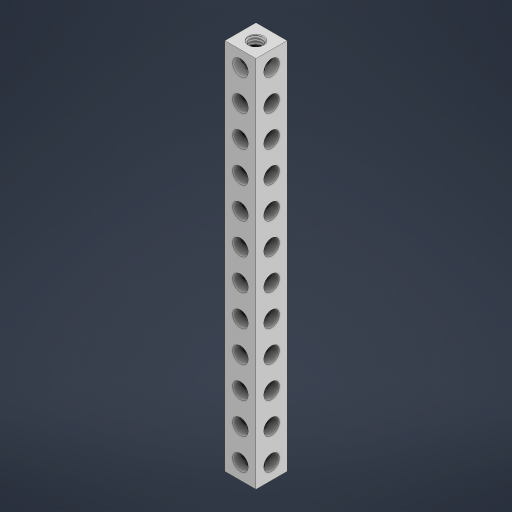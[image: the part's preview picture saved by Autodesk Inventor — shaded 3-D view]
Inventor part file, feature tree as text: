
AUTODESK INVENTOR PART (.ipt)
format: ipt  version: 2023 (Build 270158000, 158)  size: 1,371,136 bytes
history: native  units: in
note: dims shown in document units (in); Inventor stores cm internally (conversion verified against a paired STEP export)
features: mirror x1
ambient origin geometry x8: Origin, YZ Plane, XZ Plane, XY Plane, X Axis, Y Axis, Z Axis, Center Point
bodies: Solid1 (feature_tree)
feature tree (1):
  mirror  "Mirror3"
